# Revit family: Specialty_Equipment-Fiberstone_Planter-Planters_Unlimited-Volta-Low-Round
name_source: partatom
category: Specialty Equipment
units: mm (PartAtom-declared; Revit-internal decimal feet)

## family parameters
Always vertical = Yes
Cut with Voids When Loaded = No
Enable Cutting in Views = No
Maintain Annotation Orientation = No
OmniClass Number = 23.40.05.21.17
OmniClass Title = Planters
Part Type = Normal
Room Calculation Point = No
Round Connector Dimension = Use Diameter
Shared = No
Work Plane-Based = No

## types (6) — shared parameters
Assembly Code = G2050600
CD_Finish = Plastic-Fiberstone-Carlsbad-Chenza
CD_Microsite = https://www.caddetails.com
CD_Product Page URL = https://www.plantersunlimited.com
CD_Specification = https://www.plantersunlimited.com
Default Elevation = 0.0"
Description = Volta Low Round Planter
Manufacturer = Planters Unlimited
Model = Volta Low Round Planter
Type Comments = Round Planter
URL = https://www.plantersunlimited.com

## per-type parameters (varying)
| type | CD_Base Radius | CD_Diameter | CD_Height | CD_Pad Spacing | CD_Radius | CD_Radius Lip |
| 18"Dia x 18"H | 5.8" | 18.0" | 18.0" | 3.3" | 9.0" | 5.4" |
| 30"Dia x 12"H | 11.8" | 30.0" | 12.0" | 9.3" | 15.0" | 11.4" |
| 30"Dia x 22"H | 11.8" | 30.0" | 22.0" | 9.3" | 15.0" | 11.4" |
| 30"Dia x 42"H | 11.8" | 30.0" | 42.0" | 9.3" | 15.0" | 11.4" |
| 36"Dia x 60"H | 14.8" | 36.0" | 60.0" | 12.3" | 18.0" | 14.4" |
| 48"Dia x 36"H | 20.8" | 48.0" | 36.0" | 18.3" | 24.0" | 20.4" |

## geometry (parser evidence)
native form markers: Sweep x3
no freeform markers — native parametric forms only
